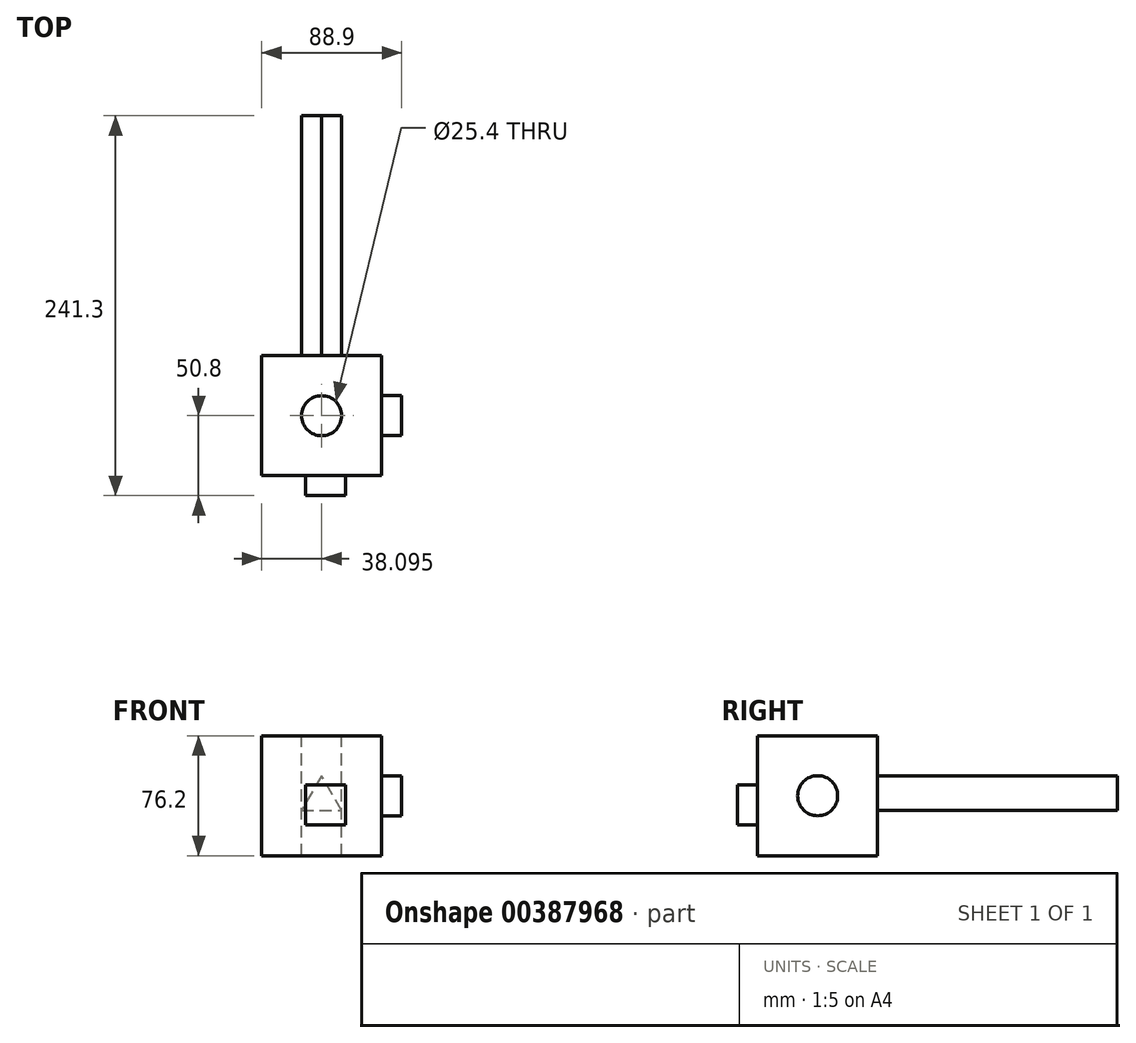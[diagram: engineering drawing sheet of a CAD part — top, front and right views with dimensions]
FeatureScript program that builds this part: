
annotation { "Feature Type Name" : "Feature", "Feature Type Description" : "" }
export const myFeature = defineFeature(function(context is Context, id is Id, definition is map)
    precondition{}
    {
        {
            var Q0;
            Q0=qCreatedBy(makeId("Front.planeOp"),FACE);
            var sketch = newSketch(context, id + "F0", { "sketchPlane" : qUnion([Q0])});
            skLineSegment(sketch, "E0.bottom", {"start": v(-32.52, 21.67) * mm, "end": v(43.68, 21.67) * mm});
            skLineSegment(sketch, "E0.top", {"start": v(-32.52, -54.53) * mm, "end": v(43.68, -54.53) * mm});
            skLineSegment(sketch, "E0.left", {"start": v(-32.52, 21.67) * mm, "end": v(-32.52, -54.53) * mm});
            skLineSegment(sketch, "E0.right", {"start": v(43.68, 21.67) * mm, "end": v(43.68, -54.53) * mm});
            skSolve(sketch);
        }
        {
            var Q0;
            Q0=makeQuery(id+"F0.imprint","IMPRINT",FACE,{"disambiguationData":[TD([[makeQuery(id+"F0.imprint","IMPRINT",EDGE,{"derivedFrom":sQuery(id+"F0.wireOp",EDGE,"E0.bottom")}),-1.0]])]});
            extrude(context, id + "F1", {"entities" : qUnion([Q0]), "depth" : 76.2 * mm});
        }
        {
            var Q0;
            Q0=makeQuery(id+"F1.opExtrude","SWEPT_FACE",FACE,{"disambiguationData":[OSD([sQuery(id+"F0.wireOp",EDGE,"E0.bottom")])]});
            var sketch = newSketch(context, id + "F2", { "sketchPlane" : qUnion([Q0])});
            skPoint(sketch, "E1", {"position": v(5.58, -38.1) * mm});
            skSolve(sketch);
        }
        {
            var Q0;
            Q0=sQuery(id+"F2.wireOp",VERTEX,"E1");
            var Q1;
            Q1=makeQuery(id+"F1.opExtrude","SWEPT_BODY",BODY,{"disambiguationData":[OSD([sQuery(id+"F0.wireOp",EDGE,"E0.bottom"),sQuery(id+"F0.wireOp",EDGE,"E0.top"),sQuery(id+"F0.wireOp",EDGE,"E0.left"),sQuery(id+"F0.wireOp",EDGE,"E0.right")])]});
            hole(context, id + "F3", {"style" : HoleStyle.SIMPLE, "endStyle" : HoleEndStyle.THROUGH, "holeDiameter" : 25.4 * mm, "isTappedThrough" : true, "tappedDepth" : 12.7 * mm, "tapClearance" : 3, "locations" : qUnion([Q0]), "scope" : qUnion([Q1])});
        }
        {
            var Q0;
            Q0=makeQuery(id+"F1.opExtrude","CAP_FACE",FACE,{"disambiguationData":[OSD([sQuery(id+"F0.wireOp",EDGE,"E0.bottom"),sQuery(id+"F0.wireOp",EDGE,"E0.top"),sQuery(id+"F0.wireOp",EDGE,"E0.left"),sQuery(id+"F0.wireOp",EDGE,"E0.right")])],"isStart":false});
            var sketch = newSketch(context, id + "F4", { "sketchPlane" : qUnion([Q0])});
            skLineSegment(sketch, "E2.bottom", {"start": v(-4.75, -9.47) * mm, "end": v(20.65, -9.47) * mm});
            skLineSegment(sketch, "E2.top", {"start": v(-4.75, -34.87) * mm, "end": v(20.65, -34.87) * mm});
            skLineSegment(sketch, "E2.left", {"start": v(-4.75, -9.47) * mm, "end": v(-4.75, -34.87) * mm});
            skLineSegment(sketch, "E2.right", {"start": v(20.65, -9.47) * mm, "end": v(20.65, -34.87) * mm});
            skSolve(sketch);
        }
        {
            var Q0;
            Q0=makeQuery(id+"F4.imprint","IMPRINT",FACE,{"disambiguationData":[TD([[makeQuery(id+"F4.imprint","IMPRINT",EDGE,{"derivedFrom":sQuery(id+"F4.wireOp",EDGE,"E2.bottom")}),-1.0]])]});
            extrude(context, id + "F5", {"entities" : qUnion([Q0]), "operationType" : NewBodyOperationType.ADD, "depth" : 12.7 * mm});
        }
        {
            var Q0;
            Q0=makeQuery(id+"F1.opExtrude","SWEPT_FACE",FACE,{"disambiguationData":[OSD([sQuery(id+"F0.wireOp",EDGE,"E0.right")])]});
            var sketch = newSketch(context, id + "F6", { "sketchPlane" : qUnion([Q0])});
            skPoint(sketch, "E3", {"position": v(-38.1, -16.43) * mm});
            skCircle(sketch, "E4", {"center": v(-38.1, -16.43) * mm, "radius": 12.7 * mm});
            skSolve(sketch);
        }
        {
            var Q0;
            Q0=makeQuery(id+"F6.imprint","IMPRINT",FACE,{"disambiguationData":[TD([[makeQuery(id+"F6.imprint","IMPRINT",EDGE,{"derivedFrom":sQuery(id+"F6.wireOp",EDGE,"E4")}),1.0]])]});
            extrude(context, id + "F7", {"entities" : qUnion([Q0]), "operationType" : NewBodyOperationType.ADD, "depth" : 12.7 * mm});
        }
        {
            var Q0;
            Q0=makeQuery(id+"F1.opExtrude","CAP_FACE",FACE,{"disambiguationData":[OSD([sQuery(id+"F0.wireOp",EDGE,"E0.bottom"),sQuery(id+"F0.wireOp",EDGE,"E0.top"),sQuery(id+"F0.wireOp",EDGE,"E0.left"),sQuery(id+"F0.wireOp",EDGE,"E0.right")])],"isStart":true});
            var sketch = newSketch(context, id + "F8", { "sketchPlane" : qUnion([Q0])});
            skCircle(sketch, "E5.cCircle", {"center": v(-5.58, -18.4) * mm, "radius": 7.33 * mm, "construction": true});
            skLineSegment(sketch, "E5.0", {"start": v(7.12, -25.73) * mm, "end": v(-18.28, -25.73) * mm});
            skLineSegment(sketch, "E5.1", {"start": v(-18.28, -25.73) * mm, "end": v(-5.58, -3.73) * mm});
            skLineSegment(sketch, "E5.2", {"start": v(-5.58, -3.73) * mm, "end": v(7.12, -25.73) * mm});
            skPoint(sketch, "E5.0.midPoint", {"position": v(-5.58, -25.73) * mm});
            skSolve(sketch);
        }
        {
            var Q0;
            Q0=makeQuery(id+"F8.imprint","IMPRINT",FACE,{"disambiguationData":[TD([[makeQuery(id+"F8.imprint","IMPRINT",EDGE,{"derivedFrom":sQuery(id+"F8.wireOp",EDGE,"E5.0")}),-1.0]])]});
            extrude(context, id + "F9", {"entities" : qUnion([Q0]), "operationType" : NewBodyOperationType.ADD, "flatOperationType" : FlatOperationType.REMOVE, "offsetDistance" : 25.4 * mm, "depth" : 152.4 * mm, "domain" : OperationDomain.MODEL});
        }
    });
